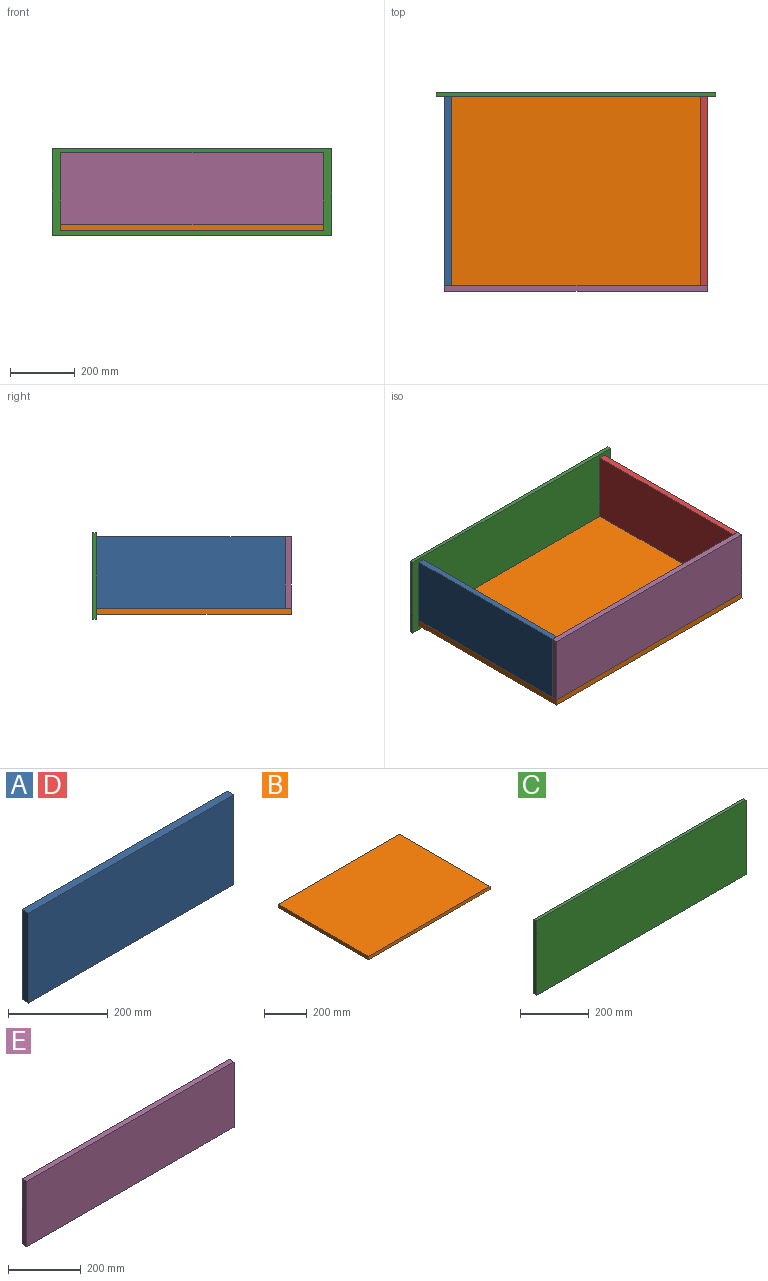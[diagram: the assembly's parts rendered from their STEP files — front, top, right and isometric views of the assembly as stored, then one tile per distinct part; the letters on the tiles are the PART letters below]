
ASSEMBLY  parts=5 mates=4
PART A: 6 faces, bbox 581x19x220 mm
  f0: plane 220x19mm, normal (-1,0,0), area 4180mm2, adj f1,f3,f4,f5
  f1: plane 581x19mm, normal (0,0,-1), area 11039mm2, adj f0,f2,f4,f5
  f2: plane 220x19mm, normal (1,0,0), area 4180mm2, adj f1,f3,f4,f5
  f3: plane 581x19mm, normal (0,0,1), area 11039mm2, adj f0,f2,f4,f5
  f4: plane 581x220mm, normal (0,-1,0), area 127820mm2, adj f0,f1,f2,f3
  f5: plane 581x220mm, normal (0,1,0), area 127820mm2, adj f0,f1,f2,f3
PART B: 6 faces, bbox 807x600x19 mm
  f0: plane 600x19mm, normal (-1,0,0), area 11400mm2, adj f1,f3,f4,f5
  f1: plane 807x19mm, normal (0,-1,0), area 15333mm2, adj f0,f2,f4,f5
  f2: plane 600x19mm, normal (1,0,0), area 11400mm2, adj f1,f3,f4,f5
  f3: plane 807x19mm, normal (0,1,0), area 15333mm2, adj f0,f2,f4,f5
  f4: plane 807x600mm, normal (0,0,1), area 484200mm2, adj f0,f1,f2,f3
  f5: plane 807x600mm, normal (0,0,-1), area 484200mm2, adj f0,f1,f2,f3
PART C: 6 faces, bbox 861x12x266 mm
  f0: plane 861x12mm, normal (0,0,1), area 10332mm2, adj f1,f3,f4,f5
  f1: plane 266x12mm, normal (-1,0,0), area 3192mm2, adj f0,f2,f4,f5
  f2: plane 861x12mm, normal (0,0,-1), area 10332mm2, adj f1,f3,f4,f5
  f3: plane 266x12mm, normal (1,0,0), area 3192mm2, adj f0,f2,f4,f5
  f4: plane 861x266mm, normal (0,-1,0), area 229026mm2, adj f0,f1,f2,f3
  f5: plane 861x266mm, normal (0,1,0), area 229026mm2, adj f0,f1,f2,f3
PART D: same geometry as A
PART E: 6 faces, bbox 807x19x220 mm
  f0: plane 220x19mm, normal (-1,0,0), area 4180mm2, adj f1,f3,f4,f5
  f1: plane 807x19mm, normal (0,0,-1), area 15333mm2, adj f0,f2,f4,f5
  f2: plane 220x19mm, normal (1,0,0), area 4180mm2, adj f1,f3,f4,f5
  f3: plane 807x19mm, normal (0,0,1), area 15333mm2, adj f0,f2,f4,f5
  f4: plane 807x220mm, normal (0,-1,0), area 177540mm2, adj f0,f1,f2,f3
  f5: plane 807x220mm, normal (0,1,0), area 177540mm2, adj f0,f1,f2,f3
PLACE A rot(axis=(0,0,-1),90deg) t=(54.81,720.26,-103.18)mm
PLACE B rot(axis=(0.33,-0.35,-0.88),0deg) t=(35.81,120.26,-122.18)mm
PLACE C rot(axis=(0,0,1),180deg) t=(439.31,720.26,-4.18)mm
PLACE D rot(axis=(0,0,1),90deg) t=(823.81,139.26,-103.18)mm
PLACE E rot(axis=(0.33,-0.35,-0.88),0deg) t=(35.81,139.26,-103.18)mm
MATE fastened B.f4 <-> E.f1  axis (0,0,1) through (439.31,120.26,-103.18)mm
MATE fastened A.f1 <-> B.f4  axis (0,0,-1) through (35.81,720.26,-103.18)mm
MATE fastened D.f1 <-> B.f4  axis (0,0,-1) through (842.81,720.26,-103.18)mm
MATE fastened B.f3 <-> C.f5  axis (0,1,0) through (439.31,720.26,-122.18)mm
